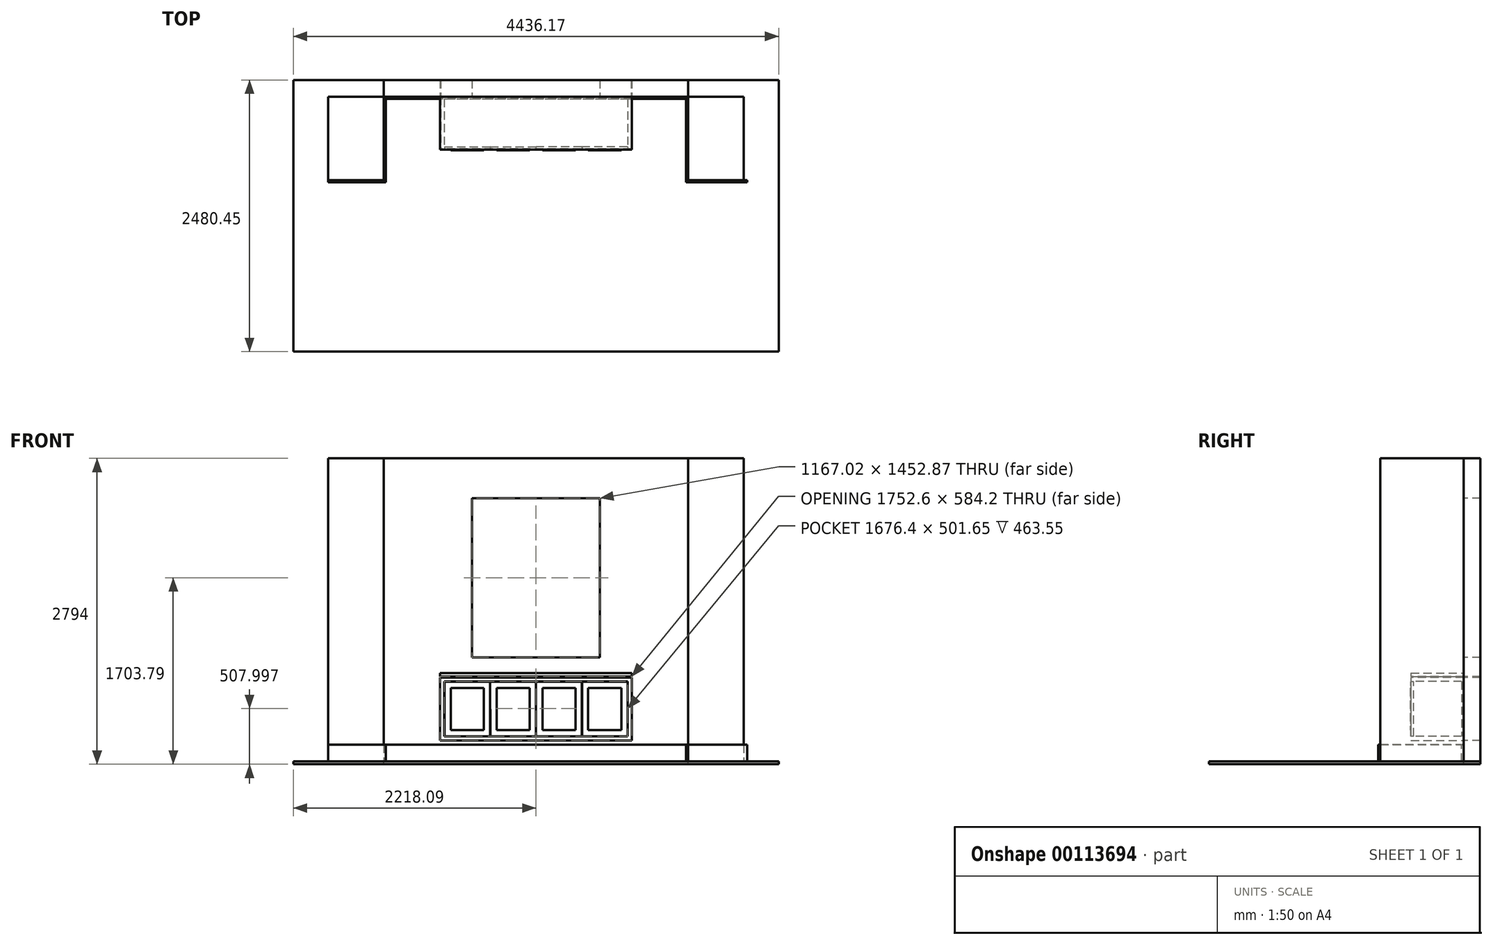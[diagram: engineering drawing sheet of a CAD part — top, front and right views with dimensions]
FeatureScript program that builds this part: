
annotation { "Feature Type Name" : "Feature", "Feature Type Description" : "" }
export const myFeature = defineFeature(function(context is Context, id is Id, definition is map)
    precondition{}
    {
        {
            var Q0;
            Q0=qCreatedBy(makeId("Front.planeOp"),FACE);
            var sketch = newSketch(context, id + "F0", { "sketchPlane" : qUnion([Q0])});
            skLineSegment(sketch, "E0.bottom", {"start": v(-443.82, 305.29) * mm, "end": v(432.48, 305.29) * mm});
            skLineSegment(sketch, "E0.top", {"start": v(-443.82, -278.91) * mm, "end": v(432.48, -278.91) * mm});
            skLineSegment(sketch, "E0.left", {"start": v(-443.82, 305.29) * mm, "end": v(-443.82, -278.91) * mm});
            skLineSegment(sketch, "E0.right", {"start": v(432.48, 305.29) * mm, "end": v(432.48, -278.91) * mm});
            skSolve(sketch);
        }
        {
            var Q0;
            Q0=makeQuery(id+"F0.imprint","IMPRINT",FACE,{"disambiguationData":[TD([[makeQuery(id+"F0.imprint","IMPRINT",EDGE,{"derivedFrom":sQuery(id+"F0.wireOp",EDGE,"E0.bottom")}),-1.0]])]});
            extrude(context, id + "F1", {"entities" : qUnion([Q0]), "depth" : 482.6 * mm});
        }
        {
            var Q0;
            Q0=makeQuery(id+"F1.opExtrude","CAP_FACE",FACE,{"disambiguationData":[OSD([sQuery(id+"F0.wireOp",EDGE,"E0.bottom"),sQuery(id+"F0.wireOp",EDGE,"E0.top"),sQuery(id+"F0.wireOp",EDGE,"E0.left"),sQuery(id+"F0.wireOp",EDGE,"E0.right")])],"isStart":false});
            var sketch = newSketch(context, id + "F2", { "sketchPlane" : qUnion([Q0])});
            skLineSegment(sketch, "E1", {"start": v(432.48, 260.84) * mm, "end": v(-405.72, 260.84) * mm});
            skLineSegment(sketch, "E2", {"start": v(-405.72, 260.84) * mm, "end": v(-405.72, -240.81) * mm});
            skLineSegment(sketch, "E3", {"start": v(-405.72, -240.81) * mm, "end": v(432.48, -240.81) * mm});
            skLineSegment(sketch, "E4", {"start": v(6.1, 305.29) * mm, "end": v(6.1, 260.84) * mm, "construction": true});
            skLineSegment(sketch, "E5", {"start": v(13.38, -278.91) * mm, "end": v(13.38, -240.81) * mm, "construction": true});
            skPoint(sketch, "E5.startSnap0", {"position": v(13.38, -240.81) * mm});
            skLineSegment(sketch, "E6", {"start": v(-405.72, 9.85) * mm, "end": v(-443.82, 9.85) * mm, "construction": true});
            skLineSegment(sketch, "E7", {"start": v(432.48, -240.81) * mm, "end": v(432.48, 260.84) * mm});
            skLineSegment(sketch, "E8.0", {"start": v(431.6, 259.06) * mm, "end": v(14.27, 259.06) * mm});
            skLineSegment(sketch, "E8.1", {"start": v(431.6, -239.04) * mm, "end": v(431.6, 259.06) * mm});
            skLineSegment(sketch, "E8.2", {"start": v(-403.94, -239.04) * mm, "end": v(12.5, -239.04) * mm});
            skLineSegment(sketch, "E8.3", {"start": v(-403.94, 259.06) * mm, "end": v(-403.94, -239.04) * mm});
            skLineSegment(sketch, "E9.0", {"start": v(15.16, -239.04) * mm, "end": v(14.27, 259.06) * mm});
            skLineSegment(sketch, "E10.0", {"start": v(12.5, -239.04) * mm, "end": v(12.5, 259.06) * mm});
            skLineSegment(sketch, "E11.trimOffspring", {"start": v(15.16, -239.04) * mm, "end": v(431.6, -239.04) * mm});
            skLineSegment(sketch, "E12.trimOffspring", {"start": v(12.5, 259.06) * mm, "end": v(-403.94, 259.06) * mm});
            skLineSegment(sketch, "E13", {"start": v(12.5, 259.06) * mm, "end": v(14.27, 259.06) * mm, "construction": true});
            skLineSegment(sketch, "E14", {"start": v(6.1, 260.84) * mm, "end": v(6.1, 259.06) * mm, "construction": true});
            skLineSegment(sketch, "E15", {"start": v(222.93, 259.06) * mm, "end": v(222.93, 260.84) * mm, "construction": true});
            skLineSegment(sketch, "E16", {"start": v(432.48, -96.88) * mm, "end": v(431.6, -96.88) * mm, "construction": true});
            skLineSegment(sketch, "E17", {"start": v(187, -239.04) * mm, "end": v(187, -240.81) * mm, "construction": true});
            skLineSegment(sketch, "E18", {"start": v(-209.7, -240.81) * mm, "end": v(-209.7, -239.04) * mm, "construction": true});
            skLineSegment(sketch, "E19", {"start": v(-403.94, -42.1) * mm, "end": v(-405.72, -42.1) * mm, "construction": true});
            skLineSegment(sketch, "E20", {"start": v(-216.87, 260.84) * mm, "end": v(-216.87, 259.06) * mm, "construction": true});
            skSolve(sketch);
        }
        {
            var Q0;
            Q0=makeQuery(id+"F2.imprint","IMPRINT",FACE,{"disambiguationData":[TD([[makeQuery(id+"F2.imprint","IMPRINT",EDGE,{"derivedFrom":sQuery(id+"F2.wireOp",EDGE,"E1")}),1.0]])]});
            extrude(context, id + "F3", {"entities" : qUnion([Q0]), "operationType" : NewBodyOperationType.REMOVE, "oppositeDirection" : true, "depth" : 463.55 * mm});
        }
        {
            var Q0;
            Q0=makeQuery(id+"F3.boolean.opBoolean","COPY",FACE,{"derivedFrom":makeQuery(id+"F3.opExtrude","SWEPT_FACE",FACE,{"disambiguationData":[OSD([sQuery(id+"F2.wireOp",EDGE,"E8.1")])]})});
            var sketch = newSketch(context, id + "F4", { "sketchPlane" : qUnion([Q0])});
            skLineSegment(sketch, "E21", {"start": v(-457.2, 259.06) * mm, "end": v(-19.05, 259.06) * mm});
            skLineSegment(sketch, "E22", {"start": v(-19.05, 259.06) * mm, "end": v(-19.05, -239.04) * mm});
            skLineSegment(sketch, "E23", {"start": v(-457.2, -239.04) * mm, "end": v(-457.2, 259.06) * mm});
            skLineSegment(sketch, "E24", {"start": v(-457.2, 7.83) * mm, "end": v(-482.6, 7.83) * mm, "construction": true});
            skSolve(sketch);
        }
        {
            var Q0;
            Q0=makeQuery(id+"F4.imprint","IMPRINT",FACE,{"disambiguationData":[TD([[makeQuery(id+"F4.imprint","IMPRINT",EDGE,{"derivedFrom":sQuery(id+"F4.wireOp",EDGE,"E21")}),1.0]])]});
            var Q1;
            Q1=makeQuery(id+"F3.boolean.opBoolean","COPY",FACE,{"derivedFrom":makeQuery(id+"F3.opExtrude","SWEPT_FACE",FACE,{"disambiguationData":[OSD([sQuery(id+"F2.wireOp",EDGE,"E8.3")])]})});
            extrude(context, id + "F5", {"entities" : qUnion([Q0]), "operationType" : NewBodyOperationType.REMOVE, "endBound" : BoundingType.UP_TO_SURFACE, "oppositeDirection" : true, "endBoundEntityFace" : qUnion([Q1]), "depth" : 25.4 * mm});
        }
        {
            var Q0;
            Q0=makeQuery(id+"F3.boolean.opBoolean","SPLIT",FACE,{"disambiguationData":[TD([makeQuery(id+"F3.opExtrude","SWEPT_FACE",FACE,{"disambiguationData":[OSD([sQuery(id+"F2.wireOp",EDGE,"E8.2")])]})])],"derivedFrom":makeQuery(id+"F1.opExtrude","CAP_FACE",FACE,{"disambiguationData":[OSD([sQuery(id+"F0.wireOp",EDGE,"E0.bottom"),sQuery(id+"F0.wireOp",EDGE,"E0.top"),sQuery(id+"F0.wireOp",EDGE,"E0.left"),sQuery(id+"F0.wireOp",EDGE,"E0.right")])],"isStart":false})});
            var sketch = newSketch(context, id + "F6", { "sketchPlane" : qUnion([Q0])});
            skLineSegment(sketch, "E25.bottom", {"start": v(-346.79, 201.9) * mm, "end": v(-44.65, 201.9) * mm});
            skLineSegment(sketch, "E25.top", {"start": v(-346.79, -181.89) * mm, "end": v(-44.65, -181.89) * mm});
            skLineSegment(sketch, "E25.left", {"start": v(-346.79, 201.9) * mm, "end": v(-346.79, -181.89) * mm});
            skLineSegment(sketch, "E25.right", {"start": v(-44.65, 201.9) * mm, "end": v(-44.65, -181.89) * mm});
            skLineSegment(sketch, "E26", {"start": v(-195.72, 259.06) * mm, "end": v(-195.72, 201.9) * mm, "construction": true});
            skLineSegment(sketch, "E27", {"start": v(-346.79, 59.25) * mm, "end": v(-403.94, 59.25) * mm, "construction": true});
            skLineSegment(sketch, "E28", {"start": v(-44.65, 33.4) * mm, "end": v(12.5, 33.4) * mm, "construction": true});
            skLineSegment(sketch, "E29", {"start": v(-195.72, -181.89) * mm, "end": v(-195.72, -239.04) * mm, "construction": true});
            skSolve(sketch);
        }
        {
            var Q0;
            Q0=makeQuery(id+"F3.boolean.opBoolean","SPLIT",FACE,{"disambiguationData":[TD([makeQuery(id+"F3.opExtrude","SWEPT_FACE",FACE,{"disambiguationData":[OSD([sQuery(id+"F2.wireOp",EDGE,"E8.0")])]})])],"derivedFrom":makeQuery(id+"F1.opExtrude","CAP_FACE",FACE,{"disambiguationData":[OSD([sQuery(id+"F0.wireOp",EDGE,"E0.bottom"),sQuery(id+"F0.wireOp",EDGE,"E0.top"),sQuery(id+"F0.wireOp",EDGE,"E0.left"),sQuery(id+"F0.wireOp",EDGE,"E0.right")])],"isStart":false})});
            var sketch = newSketch(context, id + "F7", { "sketchPlane" : qUnion([Q0])});
            skLineSegment(sketch, "E30.bottom", {"start": v(71.78, 201.9) * mm, "end": v(373.91, 201.9) * mm});
            skLineSegment(sketch, "E30.top", {"start": v(71.78, -182.4) * mm, "end": v(373.91, -182.4) * mm});
            skLineSegment(sketch, "E30.left", {"start": v(71.78, 201.9) * mm, "end": v(71.78, -182.4) * mm});
            skLineSegment(sketch, "E30.right", {"start": v(373.91, 201.9) * mm, "end": v(373.91, -182.4) * mm});
            skLineSegment(sketch, "E31", {"start": v(225.64, 259.06) * mm, "end": v(225.64, 201.9) * mm, "construction": true});
            skLineSegment(sketch, "E32", {"start": v(71.78, 58.74) * mm, "end": v(14.63, 58.74) * mm, "construction": true});
            skLineSegment(sketch, "E33", {"start": v(373.91, 32.89) * mm, "end": v(431.06, 32.89) * mm, "construction": true});
            skLineSegment(sketch, "E34", {"start": v(222.85, -182.4) * mm, "end": v(222.85, -239.54) * mm, "construction": true});
            skSolve(sketch);
        }
        {
            var Q0;
            Q0=makeQuery(id+"F6.imprint","IMPRINT",FACE,{"disambiguationData":[TD([[makeQuery(id+"F6.imprint","IMPRINT",EDGE,{"derivedFrom":sQuery(id+"F6.wireOp",EDGE,"E25.bottom")}),-1.0]])]});
            extrude(context, id + "F8", {"entities" : qUnion([Q0]), "operationType" : NewBodyOperationType.ADD, "depth" : 6.35 * mm});
        }
        {
            var Q0;
            Q0=makeQuery(id+"F7.imprint","IMPRINT",FACE,{"disambiguationData":[TD([[makeQuery(id+"F7.imprint","IMPRINT",EDGE,{"derivedFrom":sQuery(id+"F7.wireOp",EDGE,"E30.bottom")}),-1.0]])]});
            extrude(context, id + "F9", {"entities" : qUnion([Q0]), "operationType" : NewBodyOperationType.ADD, "depth" : 6.35 * mm});
        }
        {
            var Q0;
            Q0=makeQuery(id+"F1.opExtrude","SWEPT_FACE",FACE,{"disambiguationData":[OSD([sQuery(id+"F0.wireOp",EDGE,"E0.left")])]});
            var sketch = newSketch(context, id + "F10", { "sketchPlane" : qUnion([Q0])});
            skLineSegment(sketch, "E35", {"start": v(476.25, 305.29) * mm, "end": v(476.25, 295.76) * mm});
            skLineSegment(sketch, "E36", {"start": v(476.25, 295.76) * mm, "end": v(482.6, 295.76) * mm});
            skSolve(sketch);
        }
        {
            var Q0;
            {var subQ0=sQuery(id+"F10.wireOp",EDGE,"E35");Q0=makeQuery(id+"F10.imprint","IMPRINT",FACE,{"disambiguationData":[TD([[makeQuery(id+"F10.imprint","IMPRINT",EDGE,{"derivedFrom":subQ0}),1.0]])]});}
            extrude(context, id + "F11", {"entities" : qUnion([Q0]), "operationType" : NewBodyOperationType.REMOVE, "endBound" : BoundingType.UP_TO_NEXT, "oppositeDirection" : true, "depth" : 25.4 * mm});
        }
        {
            var Q0;
            Q0=makeQuery(id+"F11.boolean.opBoolean","COPY",FACE,{"derivedFrom":makeQuery(id+"F11.opExtrude","SWEPT_FACE",FACE,{"disambiguationData":[OSD([sQuery(id+"F10.wireOp",EDGE,"E35")])]})});
            var sketch = newSketch(context, id + "F12", { "sketchPlane" : qUnion([Q0])});
            skLineSegment(sketch, "E37", {"start": v(-443.82, 305.29) * mm, "end": v(-443.82, 295.76) * mm});
            skLineSegment(sketch, "E38", {"start": v(-443.82, 295.76) * mm, "end": v(-437.47, 295.76) * mm});
            skLineSegment(sketch, "E39", {"start": v(-437.47, 295.76) * mm, "end": v(-437.47, 305.29) * mm});
            skSolve(sketch);
        }
        {
            var Q0;
            {var subQ0=sQuery(id+"F12.wireOp",EDGE,"E37");Q0=makeQuery(id+"F12.imprint","IMPRINT",FACE,{"disambiguationData":[TD([[makeQuery(id+"F12.imprint","IMPRINT",EDGE,{"derivedFrom":subQ0}),1.0]])]});}
            extrude(context, id + "F13", {"entities" : qUnion([Q0]), "operationType" : NewBodyOperationType.REMOVE, "endBound" : BoundingType.UP_TO_NEXT, "oppositeDirection" : true, "depth" : 25.4 * mm});
        }
        {
            var Q0;
            Q0=makeQuery(id+"F5.boolean.opBoolean","SPLIT",BODY,{"disambiguationData":[OD(1.0)],"derivedFrom":makeQuery(id+"F1.opExtrude","SWEPT_BODY",BODY,{"disambiguationData":[OSD([sQuery(id+"F0.wireOp",EDGE,"E0.bottom"),sQuery(id+"F0.wireOp",EDGE,"E0.top"),sQuery(id+"F0.wireOp",EDGE,"E0.left"),sQuery(id+"F0.wireOp",EDGE,"E0.right")])]})});
            var Q1;
            Q1=makeQuery(id+"F5.boolean.opBoolean","SPLIT",BODY,{"disambiguationData":[OD(2.0)],"derivedFrom":makeQuery(id+"F1.opExtrude","SWEPT_BODY",BODY,{"disambiguationData":[OSD([sQuery(id+"F0.wireOp",EDGE,"E0.bottom"),sQuery(id+"F0.wireOp",EDGE,"E0.top"),sQuery(id+"F0.wireOp",EDGE,"E0.left"),sQuery(id+"F0.wireOp",EDGE,"E0.right")])]})});
            var Q2;
            Q2=makeQuery(id+"F5.boolean.opBoolean","SPLIT",BODY,{"disambiguationData":[OD(0.0)],"derivedFrom":makeQuery(id+"F1.opExtrude","SWEPT_BODY",BODY,{"disambiguationData":[OSD([sQuery(id+"F0.wireOp",EDGE,"E0.bottom"),sQuery(id+"F0.wireOp",EDGE,"E0.top"),sQuery(id+"F0.wireOp",EDGE,"E0.left"),sQuery(id+"F0.wireOp",EDGE,"E0.right")])]})});
            var Q3;
            {var subQ0=sQuery(id+"F0.wireOp",EDGE,"E0.right");Q3=makeQuery(id+"FuZBYlhMW1sXyOV_1.boolean.opBoolean","MERGE",FACE,{"derivedFrom":[makeQuery(id+"F1.opExtrude","SWEPT_FACE",FACE,{"disambiguationData":[OSD([subQ0])]}),makeQuery(id+"FuZBYlhMW1sXyOV_1.opExtrude","CAP_FACE",FACE,{"disambiguationData":[OSD([subQ0])],"isStart":false})]});}
            mirror(context, id + "F14", {"operationType" : NewBodyOperationType.ADD, "entities" : qUnion([Q0, Q1, Q2]), "mirrorPlane" : qUnion([Q3])});
        }
        {
            var Q0;
            {var subQ0=makeQuery(id+"FuZBYlhMW1sXyOV_1.boolean.opBoolean","MERGE",FACE,{"derivedFrom":[makeQuery(id+"F1.opExtrude","CAP_FACE",FACE,{"disambiguationData":[OSD([sQuery(id+"F0.wireOp",EDGE,"E0.bottom"),sQuery(id+"F0.wireOp",EDGE,"E0.top"),sQuery(id+"F0.wireOp",EDGE,"E0.left"),sQuery(id+"F0.wireOp",EDGE,"E0.right")])],"isStart":true}),makeQuery(id+"FuZBYlhMW1sXyOV_1.opExtrude","SWEPT_FACE",FACE,{"disambiguationData":[OSD([sQuery(id+"FYhYcJRtpV1afrZ_1.wireOp",EDGE,"LgGKqngq-pQfP-o0Gm-Cr1w-83hMu0TkOIDQ")])]})]});Q0=makeQuery(id+"F14.boolean.opBoolean","MERGE",FACE,{"derivedFrom":[subQ0,makeQuery(id+"F14.opPattern","COPY",FACE,{"derivedFrom":subQ0,"instanceName":"1"})]});}
            var sketch = newSketch(context, id + "F15", { "sketchPlane" : qUnion([Q0])});
            skLineSegment(sketch, "E40", {"start": v(-432.48, -278.91) * mm, "end": v(-432.48, -469.41) * mm, "construction": true});
            skLineSegment(sketch, "E41", {"start": v(-432.48, -469.41) * mm, "end": v(-1823.02, -469.41) * mm});
            skLineSegment(sketch, "E42", {"start": v(-1823.02, -469.41) * mm, "end": v(-1823.02, 2299.19) * mm});
            skLineSegment(sketch, "E43", {"start": v(-1823.02, 2299.19) * mm, "end": v(958.05, 2299.19) * mm});
            skLineSegment(sketch, "E44", {"start": v(958.05, 2299.19) * mm, "end": v(958.05, -469.41) * mm});
            skLineSegment(sketch, "E45", {"start": v(-432.48, -469.41) * mm, "end": v(958.05, -469.41) * mm});
            skLineSegment(sketch, "E46", {"start": v(-432.48, 482.54) * mm, "end": v(151.02, 482.54) * mm});
            skLineSegment(sketch, "E47", {"start": v(151.02, 482.54) * mm, "end": v(151.02, 1935.41) * mm});
            skLineSegment(sketch, "E48", {"start": v(151.02, 1935.41) * mm, "end": v(-1016, 1935.41) * mm});
            skLineSegment(sketch, "E49", {"start": v(-1016, 1935.41) * mm, "end": v(-1016, 482.54) * mm});
            skLineSegment(sketch, "E50", {"start": v(-432.48, 482.54) * mm, "end": v(-1016, 482.54) * mm});
            skSolve(sketch);
        }
        {
            var Q0;
            Q0=makeQuery(id+"F15.imprint","IMPRINT",FACE,{"disambiguationData":[TD([[makeQuery(id+"F15.imprint","IMPRINT",EDGE,{"derivedFrom":sQuery(id+"F15.wireOp",EDGE,"E41")}),-1.0]])]});
            extrude(context, id + "F16", {"entities" : qUnion([Q0]), "depth" : 152.4 * mm});
        }
        {
            var Q0;
            Q0=makeQuery(id+"F16.opExtrude","CAP_FACE",FACE,{"disambiguationData":[OSD([sQuery(id+"F0.wireOp",EDGE,"E0.bottom"),sQuery(id+"F0.wireOp",EDGE,"E0.top"),sQuery(id+"F0.wireOp",EDGE,"E0.left"),sQuery(id+"F0.wireOp",EDGE,"E0.right"),sQuery(id+"F12.wireOp",EDGE,"E38"),sQuery(id+"F12.wireOp",EDGE,"E39"),sQuery(id+"F15.wireOp",EDGE,"E41"),sQuery(id+"F15.wireOp",EDGE,"E42"),sQuery(id+"F15.wireOp",EDGE,"E43"),sQuery(id+"F15.wireOp",EDGE,"E44"),sQuery(id+"F15.wireOp",EDGE,"E45"),sQuery(id+"F15.wireOp",EDGE,"E46"),sQuery(id+"F15.wireOp",EDGE,"E47"),sQuery(id+"F15.wireOp",EDGE,"E48"),sQuery(id+"F15.wireOp",EDGE,"E49"),sQuery(id+"F15.wireOp",EDGE,"E50")])],"isStart":true});
            var sketch = newSketch(context, id + "F17", { "sketchPlane" : qUnion([Q0])});
            skLineSegment(sketch, "E51", {"start": v(-443.82, 305.29) * mm, "end": v(-443.82, 337.04) * mm});
            skLineSegment(sketch, "E52", {"start": v(-443.82, 337.04) * mm, "end": v(1308.78, 337.04) * mm});
            skLineSegment(sketch, "E53", {"start": v(1308.78, 337.04) * mm, "end": v(1308.78, 305.29) * mm});
            skLineSegment(sketch, "E54", {"start": v(1308.78, 305.29) * mm, "end": v(-443.82, 305.29) * mm});
            skSolve(sketch);
        }
        {
            var Q0;
            {var subQ9=sQuery(id+"F17.wireOp",EDGE,"E51");Q0=makeQuery(id+"F17.imprint","IMPRINT",FACE,{"disambiguationData":[TD([[makeQuery(id+"F17.imprint","IMPRINT",EDGE,{"derivedFrom":subQ9}),-1.0]])]});}
            extrude(context, id + "F18", {"entities" : qUnion([Q0]), "depth" : 482.6 * mm});
        }
        {
            var Q0;
            Q0=makeQuery(id+"F16.opExtrude","SWEPT_FACE",FACE,{"disambiguationData":[OSD([sQuery(id+"F15.wireOp",EDGE,"E42")])]});
            var sketch = newSketch(context, id + "F19", { "sketchPlane" : qUnion([Q0])});
            skLineSegment(sketch, "E55", {"start": v(152.4, 2299.19) * mm, "end": v(-762, 2299.19) * mm});
            skLineSegment(sketch, "E56", {"start": v(-762, 2299.19) * mm, "end": v(-762, -469.41) * mm});
            skLineSegment(sketch, "E57", {"start": v(152.4, -469.41) * mm, "end": v(-762, -469.41) * mm});
            skSolve(sketch);
        }
        {
            var Q0;
            {var subQ2=sQuery(id+"F19.wireOp",EDGE,"E56");Q0=makeQuery(id+"F19.imprint","IMPRINT",FACE,{"disambiguationData":[TD([[makeQuery(id+"F19.imprint","IMPRINT",EDGE,{"derivedFrom":subQ2}),1.0]])]});}
            extrude(context, id + "F20", {"entities" : qUnion([Q0]), "depth" : 508 * mm});
        }
        {
            var Q0;
            Q0=makeQuery(id+"F16.opExtrude","SWEPT_FACE",FACE,{"disambiguationData":[OSD([sQuery(id+"F15.wireOp",EDGE,"E44")])]});
            var sketch = newSketch(context, id + "F21", { "sketchPlane" : qUnion([Q0])});
            skLineSegment(sketch, "E58", {"start": v(-152.4, 2299.19) * mm, "end": v(762, 2299.19) * mm});
            skLineSegment(sketch, "E59", {"start": v(762, 2299.19) * mm, "end": v(762, -469.41) * mm});
            skLineSegment(sketch, "E60", {"start": v(762, -469.41) * mm, "end": v(-152.4, -469.41) * mm});
            skLineSegment(sketch, "E61", {"start": v(-152.4, 2299.19) * mm, "end": v(-152.4, -469.41) * mm});
            skSolve(sketch);
        }
        {
            var Q0;
            {var subQ2=sQuery(id+"F21.wireOp",EDGE,"E59");Q0=makeQuery(id+"F21.imprint","IMPRINT",FACE,{"disambiguationData":[TD([[makeQuery(id+"F21.imprint","IMPRINT",EDGE,{"derivedFrom":subQ2}),-1.0]])]});}
            extrude(context, id + "F22", {"entities" : qUnion([Q0]), "depth" : 508 * mm});
        }
        {
            var Q0;
            Q0=makeQuery(id+"F16.opExtrude","SWEPT_FACE",FACE,{"disambiguationData":[OSD([sQuery(id+"F15.wireOp",EDGE,"E41"),sQuery(id+"F15.wireOp",EDGE,"E45")])]});
            var sketch = newSketch(context, id + "F23", { "sketchPlane" : qUnion([Q0])});
            skLineSegment(sketch, "E62", {"start": v(-958.05, -152.4) * mm, "end": v(1823.02, -152.4) * mm});
            skLineSegment(sketch, "E63", {"start": v(1823.02, -152.4) * mm, "end": v(2650.57, -152.4) * mm});
            skLineSegment(sketch, "E64", {"start": v(2650.57, -152.4) * mm, "end": v(2650.57, 2328.05) * mm});
            skLineSegment(sketch, "E65", {"start": v(2650.57, 2328.05) * mm, "end": v(-1785.6, 2328.05) * mm});
            skLineSegment(sketch, "E66", {"start": v(-1785.6, 2328.05) * mm, "end": v(-1785.6, -152.4) * mm});
            skLineSegment(sketch, "E67", {"start": v(-958.05, -152.4) * mm, "end": v(-1785.6, -152.4) * mm});
            skSolve(sketch);
        }
        {
            var Q0;
            Q0=makeQuery(id+"F23.imprint","IMPRINT",FACE,{"disambiguationData":[TD([[makeQuery(id+"F23.imprint","IMPRINT",EDGE,{"derivedFrom":sQuery(id+"F23.wireOp",EDGE,"E63")}),1.0]])]});
            extrude(context, id + "F24", {"entities" : qUnion([Q0]), "depth" : 25.4 * mm});
        }
        {
            var Q0;
            Q0=makeQuery(id+"F16.opExtrude","CAP_FACE",FACE,{"disambiguationData":[OSD([sQuery(id+"F0.wireOp",EDGE,"E0.bottom"),sQuery(id+"F0.wireOp",EDGE,"E0.top"),sQuery(id+"F0.wireOp",EDGE,"E0.left"),sQuery(id+"F0.wireOp",EDGE,"E0.right"),sQuery(id+"F10.wireOp",EDGE,"E35"),sQuery(id+"FYhYcJRtpV1afrZ_1.wireOp",EDGE,"LgGKqngq-pQfP-o0Gm-Cr1w-83hMu0TkOIDQ"),sQuery(id+"FYhYcJRtpV1afrZ_1.wireOp",EDGE,"wtlT6dZa-HLd2-9Hce-N2Jz-HCNb6eQw7Zcr"),sQuery(id+"F12.wireOp",EDGE,"E38"),sQuery(id+"F12.wireOp",EDGE,"E39"),sQuery(id+"F15.wireOp",EDGE,"E41"),sQuery(id+"F15.wireOp",EDGE,"E42"),sQuery(id+"F15.wireOp",EDGE,"E43"),sQuery(id+"F15.wireOp",EDGE,"E44"),sQuery(id+"F15.wireOp",EDGE,"E45"),sQuery(id+"F15.wireOp",EDGE,"E46"),sQuery(id+"F15.wireOp",EDGE,"E47"),sQuery(id+"F15.wireOp",EDGE,"E48"),sQuery(id+"F15.wireOp",EDGE,"E49"),sQuery(id+"F15.wireOp",EDGE,"E50")])],"isStart":true});
            var sketch = newSketch(context, id + "F25", { "sketchPlane" : qUnion([Q0])});
            skLineSegment(sketch, "E68", {"start": v(1823.02, -469.41) * mm, "end": v(1823.02, -317.01) * mm});
            skLineSegment(sketch, "E69", {"start": v(1823.02, -317.01) * mm, "end": v(-958.05, -317.01) * mm});
            skLineSegment(sketch, "E70", {"start": v(-958.05, -469.41) * mm, "end": v(1823.02, -469.41) * mm});
            skSolve(sketch);
        }
        {
            var Q0;
            Q0=makeQuery(id+"F25.imprint","IMPRINT",FACE,{"disambiguationData":[TD([[makeQuery(id+"F25.imprint","IMPRINT",EDGE,{"derivedFrom":sQuery(id+"F25.wireOp",EDGE,"E68")}),1.0]])]});
            extrude(context, id + "F26", {"entities" : qUnion([Q0]), "depth" : 19.05 * mm});
        }
        {
            var Q0;
            Q0=makeQuery(id+"F20.opExtrude","CAP_FACE",FACE,{"disambiguationData":[OSD([sQuery(id+"F15.wireOp",EDGE,"E42"),sQuery(id+"F19.wireOp",EDGE,"E55"),sQuery(id+"F19.wireOp",EDGE,"E56"),sQuery(id+"F19.wireOp",EDGE,"E57")])],"isStart":true});
            var sketch = newSketch(context, id + "F27", { "sketchPlane" : qUnion([Q0])});
            skLineSegment(sketch, "E71", {"start": v(0, -469.41) * mm, "end": v(0, -317.01) * mm});
            skLineSegment(sketch, "E72", {"start": v(0, -317.01) * mm, "end": v(762, -317.01) * mm});
            skLineSegment(sketch, "E73", {"start": v(762, -317.01) * mm, "end": v(762, -469.41) * mm});
            skLineSegment(sketch, "E74", {"start": v(762, -469.41) * mm, "end": v(0, -469.41) * mm});
            skSolve(sketch);
        }
        {
            var Q0;
            Q0=makeQuery(id+"F27.imprint","IMPRINT",FACE,{"disambiguationData":[TD([[makeQuery(id+"F27.imprint","IMPRINT",EDGE,{"derivedFrom":sQuery(id+"F27.wireOp",EDGE,"E71")}),-1.0]])]});
            extrude(context, id + "F28", {"entities" : qUnion([Q0]), "depth" : 19.05 * mm});
        }
        {
            var Q0;
            Q0=makeQuery(id+"F28.opExtrude","SWEPT_FACE",FACE,{"disambiguationData":[OSD([sQuery(id+"F27.wireOp",EDGE,"E73")])]});
            var sketch = newSketch(context, id + "F29", { "sketchPlane" : qUnion([Q0])});
            skLineSegment(sketch, "E75", {"start": v(1803.97, -317.01) * mm, "end": v(2361.74, -317.01) * mm});
            skLineSegment(sketch, "E76", {"start": v(2361.74, -317.01) * mm, "end": v(2361.74, -469.41) * mm});
            skPoint(sketch, "E76.endSnap0", {"position": v(1813.5, -469.41) * mm});
            skLineSegment(sketch, "E77", {"start": v(2361.74, -469.41) * mm, "end": v(1803.97, -469.41) * mm});
            skLineSegment(sketch, "E78", {"start": v(1803.97, -469.41) * mm, "end": v(1803.97, -317.01) * mm});
            skSolve(sketch);
        }
        {
            var Q0;
            {var subQ2=sQuery(id+"F29.wireOp",EDGE,"E76");Q0=makeQuery(id+"F29.imprint","IMPRINT",FACE,{"disambiguationData":[TD([[makeQuery(id+"F29.imprint","IMPRINT",EDGE,{"derivedFrom":subQ2}),-1.0]])]});}
            extrude(context, id + "F30", {"entities" : qUnion([Q0]), "depth" : 19.05 * mm});
        }
        {
            var Q0;
            Q0=makeQuery(id+"F28.opExtrude","SWEPT_FACE",FACE,{"disambiguationData":[OSD([sQuery(id+"F27.wireOp",EDGE,"E73")])]});
            var sketch = newSketch(context, id + "F31", { "sketchPlane" : qUnion([Q0])});
            skSolve(sketch);
        }
        {
            var Q0;
            {var subQ0=sQuery(id+"F27.wireOp",EDGE,"E73");Q0=makeQuery(id+"F31.imprint","IMPRINT",FACE,{"disambiguationData":[TD([[makeQuery(id+"F31.imprint","IMPRINT",EDGE,{"derivedFrom":makeQuery(id+"F28.opExtrude","CAP_EDGE",EDGE,{"disambiguationData":[OSD([subQ0])],"isStart":true})}),-1.0]])]});}
            var Q1;
            Q1=makeQuery(id+"F30.opExtrude","CAP_FACE",FACE,{"disambiguationData":[OSD([sQuery(id+"F27.wireOp",EDGE,"E73"),sQuery(id+"F29.wireOp",EDGE,"E75"),sQuery(id+"F29.wireOp",EDGE,"E76"),sQuery(id+"F29.wireOp",EDGE,"E77")])],"isStart":false});
            extrude(context, id + "F32", {"entities" : qUnion([Q0]), "endBound" : BoundingType.UP_TO_SURFACE, "endBoundEntityFace" : qUnion([Q1]), "depth" : 25.4 * mm});
        }
        {
            var Q0;
            Q0=makeQuery(id+"F26.opExtrude","CAP_FACE",FACE,{"disambiguationData":[OSD([sQuery(id+"F15.wireOp",EDGE,"E44"),sQuery(id+"F25.wireOp",EDGE,"E68"),sQuery(id+"F25.wireOp",EDGE,"E69"),sQuery(id+"F25.wireOp",EDGE,"E70")])],"isStart":false});
            var sketch = newSketch(context, id + "F33", { "sketchPlane" : qUnion([Q0])});
            skLineSegment(sketch, "E79", {"start": v(-958.05, -469.41) * mm, "end": v(-958.05, -317.01) * mm});
            skLineSegment(sketch, "E80", {"start": v(-958.05, -317.01) * mm, "end": v(-939, -317.01) * mm});
            skLineSegment(sketch, "E81", {"start": v(-939, -317.01) * mm, "end": v(-939, -469.41) * mm});
            skLineSegment(sketch, "E82", {"start": v(-939, -469.41) * mm, "end": v(-958.05, -469.41) * mm});
            skSolve(sketch);
        }
        {
            var Q0;
            Q0=makeQuery(id+"F33.imprint","IMPRINT",FACE,{"disambiguationData":[TD([[makeQuery(id+"F33.imprint","IMPRINT",EDGE,{"derivedFrom":sQuery(id+"F33.wireOp",EDGE,"E79")}),1.0]])]});
            var Q1;
            Q1=makeQuery(id+"F22.opExtrude","SWEPT_FACE",FACE,{"disambiguationData":[OSD([sQuery(id+"F21.wireOp",EDGE,"E59")])]});
            extrude(context, id + "F34", {"entities" : qUnion([Q0]), "endBound" : BoundingType.UP_TO_SURFACE, "endBoundEntityFace" : qUnion([Q1]), "depth" : 25.4 * mm});
        }
        {
            var Q0;
            Q0=makeQuery(id+"F22.opExtrude","SWEPT_FACE",FACE,{"disambiguationData":[OSD([sQuery(id+"F21.wireOp",EDGE,"E59")])]});
            var sketch = newSketch(context, id + "F35", { "sketchPlane" : qUnion([Q0])});
            skLineSegment(sketch, "E83", {"start": v(-958.05, -469.41) * mm, "end": v(-958.05, -317.01) * mm});
            skLineSegment(sketch, "E84", {"start": v(-958.05, -317.01) * mm, "end": v(-1466.05, -317.01) * mm});
            skLineSegment(sketch, "E85", {"start": v(-1466.05, -317.01) * mm, "end": v(-1466.05, -469.41) * mm});
            skLineSegment(sketch, "E86", {"start": v(-1466.05, -469.41) * mm, "end": v(-958.05, -469.41) * mm});
            skSolve(sketch);
        }
        {
            var Q0;
            Q0=sQuery(id+"F35.wireOp",EDGE,"E85");
            extrude(context, id + "F36", {"bodyType" : ToolBodyType.SURFACE, "surfaceEntities" : qUnion([Q0]), "depth" : 19.05 * mm});
        }
        {
            var Q0;
            Q0=makeQuery(id+"F36.opExtrude","SWEPT_FACE",FACE,{"disambiguationData":[OSD([sQuery(id+"F35.wireOp",EDGE,"E85")])]});
            var Q1;
            Q1=makeQuery(id+"F34.opExtrude","SWEPT_FACE",FACE,{"disambiguationData":[OSD([sQuery(id+"F33.wireOp",EDGE,"E81")])]});
            extrude(context, id + "F37", {"entities" : qUnion([Q0]), "endBound" : BoundingType.UP_TO_SURFACE, "oppositeDirection" : true, "endBoundEntityFace" : qUnion([Q1]), "depth" : 25.4 * mm});
        }
    });
